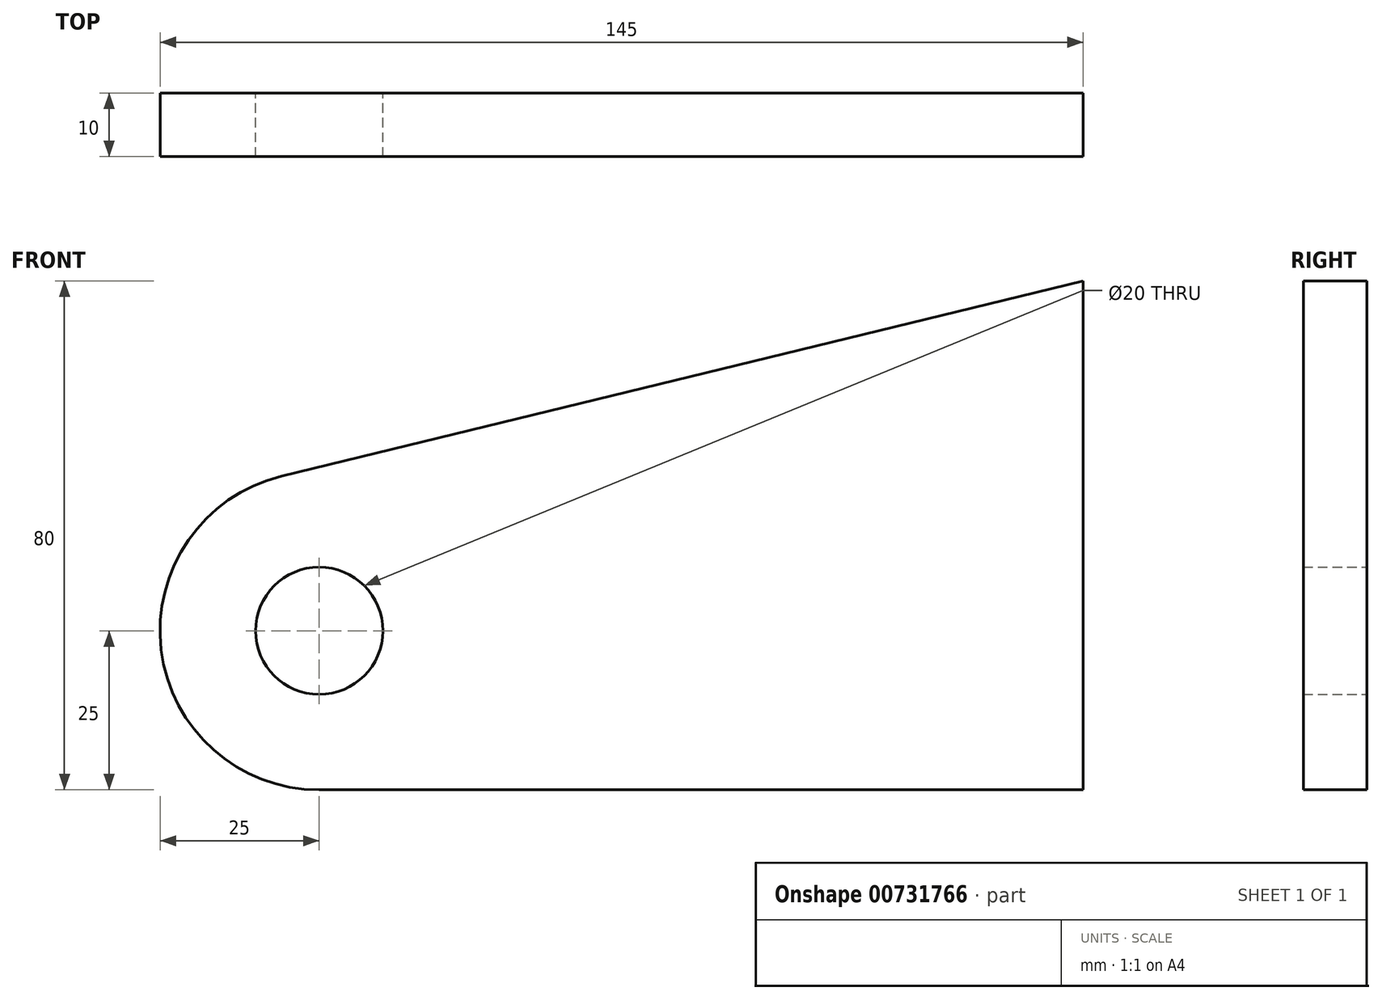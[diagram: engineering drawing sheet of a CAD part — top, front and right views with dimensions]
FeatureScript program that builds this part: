
annotation { "Feature Type Name" : "Feature", "Feature Type Description" : "" }
export const myFeature = defineFeature(function(context is Context, id is Id, definition is map)
    precondition{}
    {
        {
            var Q0;
            Q0=qCreatedBy(makeId("Front.planeOp"),FACE);
            var sketch = newSketch(context, id + "F0", { "sketchPlane" : qUnion([Q0])});
            skCircle(sketch, "E0", {"center": v(0, 0) * mm, "radius": 10 * mm});
            skLineSegment(sketch, "E1", {"start": v(0, -25) * mm, "end": v(120, -25) * mm});
            skLineSegment(sketch, "E2", {"start": v(120, -25) * mm, "end": v(120, 55) * mm});
            skArc(sketch, "E3", {"start": v(-5.92, 24.29) * mm, "mid": v(-24.82, -2.98) * mm, "end": v(0, -25) * mm});
            skLineSegment(sketch, "E4", {"start": v(-5.92, 24.29) * mm, "end": v(120, 55) * mm});
            skSolve(sketch);
        }
        {
            var Q0;
            Q0=makeQuery(id+"F0.imprint","IMPRINT",FACE,{"disambiguationData":[TD([[makeQuery(id+"F0.imprint","IMPRINT",EDGE,{"derivedFrom":sQuery(id+"F0.wireOp",EDGE,"E0")}),-1.0]])]});
            extrude(context, id + "F1", {"entities" : qUnion([Q0]), "depth" : 10 * mm, "offsetDistance" : 25 * mm});
        }
    });
